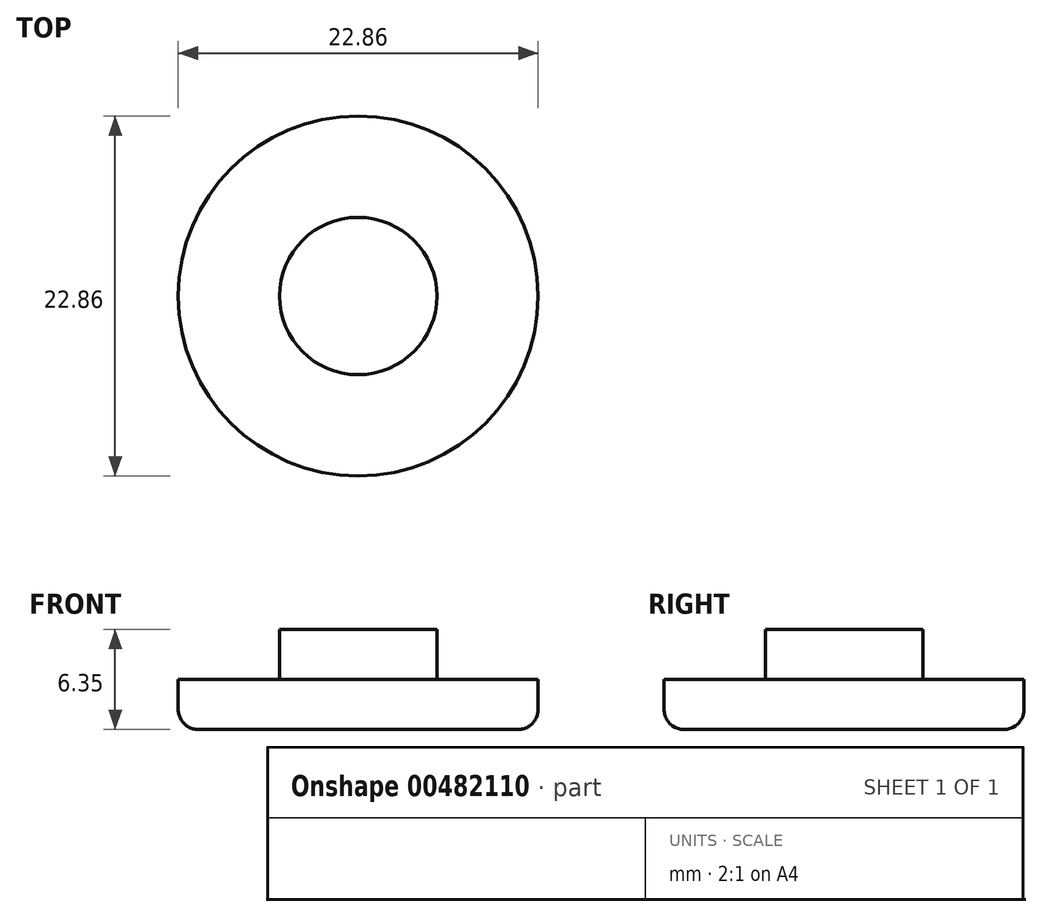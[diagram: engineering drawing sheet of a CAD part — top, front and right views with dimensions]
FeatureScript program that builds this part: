
annotation { "Feature Type Name" : "Feature", "Feature Type Description" : "" }
export const myFeature = defineFeature(function(context is Context, id is Id, definition is map)
    precondition{}
    {
        {
            var Q0;
            Q0=qCreatedBy(makeId("Top.planeOp"),FACE);
            var sketch = newSketch(context, id + "F0", { "sketchPlane" : qUnion([Q0])});
            skCircle(sketch, "E0", {"center": v(0, 0) * mm, "radius": 11.43 * mm});
            skCircle(sketch, "E1", {"center": v(0, 0) * mm, "radius": 5 * mm});
            skSolve(sketch);
        }
        {
            var Q0;
            Q0=makeQuery(id+"F0.imprint","IMPRINT",FACE,{"disambiguationData":[TD([[makeQuery(id+"F0.imprint","IMPRINT",EDGE,{"derivedFrom":sQuery(id+"F0.wireOp",EDGE,"E1")}),1.0]])]});
            extrude(context, id + "F1", {"entities" : qUnion([Q0]), "depth" : 6.35 * mm});
        }
        {
            var Q0;
            Q0=qSketchRegion(id+"F0",true);
            extrude(context, id + "F2", {"entities" : qUnion([Q0]), "operationType" : NewBodyOperationType.ADD, "depth" : 3.17 * mm});
        }
        {
            var Q0;
            Q0=makeQuery(id+"F2.opExtrude","CAP_EDGE",EDGE,{"disambiguationData":[OSD([sQuery(id+"F0.wireOp",EDGE,"E0")])],"isStart":true});
            fillet(context, id + "F3", {"entities" : qUnion([Q0]), "radius" : 1.27 * mm, "tangentPropagation" : true, "allowEdgeOverflow" : false});
        }
    });
